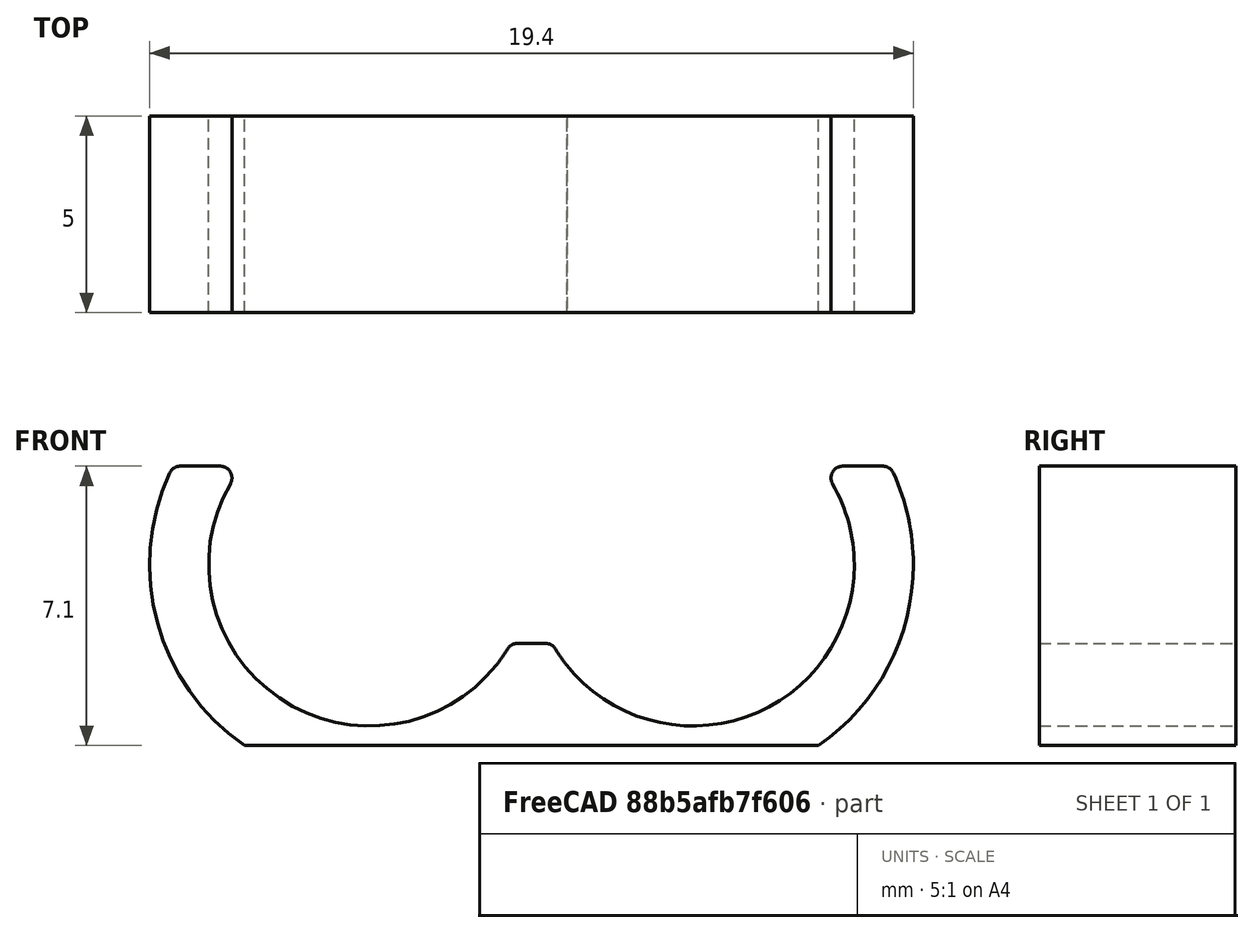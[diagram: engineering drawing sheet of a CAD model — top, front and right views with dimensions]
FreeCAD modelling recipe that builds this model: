
FCSTD DOCUMENT  (FreeCAD 0.18.4R)
Label: CapClip2
License: All rights reserved
LicenseURL: http://en.wikipedia.org/wiki/All_rights_reserved
objects: Part::Box×5, Part::Cut×5, Part::Cylinder×4, Part::MultiFuse×3, Part::Fillet×2, Mesh::Feature×1
note: 19 computed .brp shape members not serialized (recipe doc carries the construction recipe); baked Part::Feature solids carry a one-line shape summary decoded from their .brp

FEATURE [Part::Box] Box  label="Würfel"
  AttacherType = Attacher::AttachEngine3D
  Height = 1
  Length = 15
  Placement = pos=(-3.5,0,-5.6) rot=(0,0,1;0rad)
  Width = 5
FEATURE [Part::Cylinder] Cylinder  label="Zylinder"
  Angle = 360
  AttacherType = Attacher::AttachEngine3D
  Height = 5
  Radius = 5.6
FEATURE [Part::Cylinder] Cylinder001  label="Zylinder001"
  Angle = 360
  AttacherType = Attacher::AttachEngine3D
  Height = 5
  Radius = 4.1
FEATURE [Part::Box] Box001  label="Würfel001"
  AttacherType = Attacher::AttachEngine3D
  Height = 5
  Length = 12
  Placement = pos=(-6,-12.5,0) rot=(0,0,1;0rad)
  Width = 10
FEATURE [Part::Box] Box002  label="Würfel002"
  AttacherType = Attacher::AttachEngine3D
  Height = 5
  Length = 10
  Placement = pos=(0,-8,0) rot=(0,0,1;0rad)
  Width = 10
FEATURE [Part::Cylinder] Cylinder002  label="Zylinder002"
  Angle = 360
  AttacherType = Attacher::AttachEngine3D
  Height = 5
  Placement = pos=(8.2,0,0) rot=(0,0,1;0rad)
  Radius = 4.1
FEATURE [Part::Cylinder] Cylinder003  label="Zylinder003"
  Angle = 360
  AttacherType = Attacher::AttachEngine3D
  Height = 5
  Placement = pos=(8.2,0,0) rot=(0,0,1;0rad)
  Radius = 5.6
FEATURE [Part::Box] Box003  label="Würfel003"
  AttacherType = Attacher::AttachEngine3D
  Height = 5
  Length = 12
  Placement = pos=(2,-12.5,0) rot=(0,0,1;0rad)
  Width = 10
FEATURE [Part::Cut] Cut
  Base = -> Cylinder003
  Tool = -> Box003
FEATURE [Part::Cut] Cut001
  Base = -> Cylinder
  Tool = -> Box001
FEATURE [Part::MultiFuse] Fusion
  Shapes = -> [Cut,Cut001]
FEATURE [Part::Cut] Cut002
  Base = -> Fusion
  Tool = -> Box002
FEATURE [Part::MultiFuse] Fusion001
  Shapes = -> [Cylinder001,Cylinder002]
FEATURE [Part::Cut] Cut003
  Base = -> Cut002
  Tool = -> Fusion001
FEATURE [Part::Fillet] Fillet
  Base = -> Cut003
  Edges = 2 edges r=0.3: [Edge22,Edge35]
FEATURE [Part::Fillet] Fillet001
  Base = -> Fillet
  Edges = 4 edges r=0.3: [Edge25,Edge34,Edge38,Edge41]
  Placement = pos=(0,0,0) rot=(-1,0,0;1.5708rad)
FEATURE [Part::Box] Box004  label="Würfel004"
  AttacherType = Attacher::AttachEngine3D
  Height = 2
  Length = 2
  Placement = pos=(3,0,-5) rot=(0,0,1;0rad)
  Width = 5
FEATURE [Part::MultiFuse] Fusion002
  Shapes = -> [Fillet001,Box004]
FEATURE [Part::Cut] Cut004
  Base = -> Fusion002
  Tool = -> Box
FEATURE [Mesh::Feature] Mesh  label="Cut004 (Meshed)"
